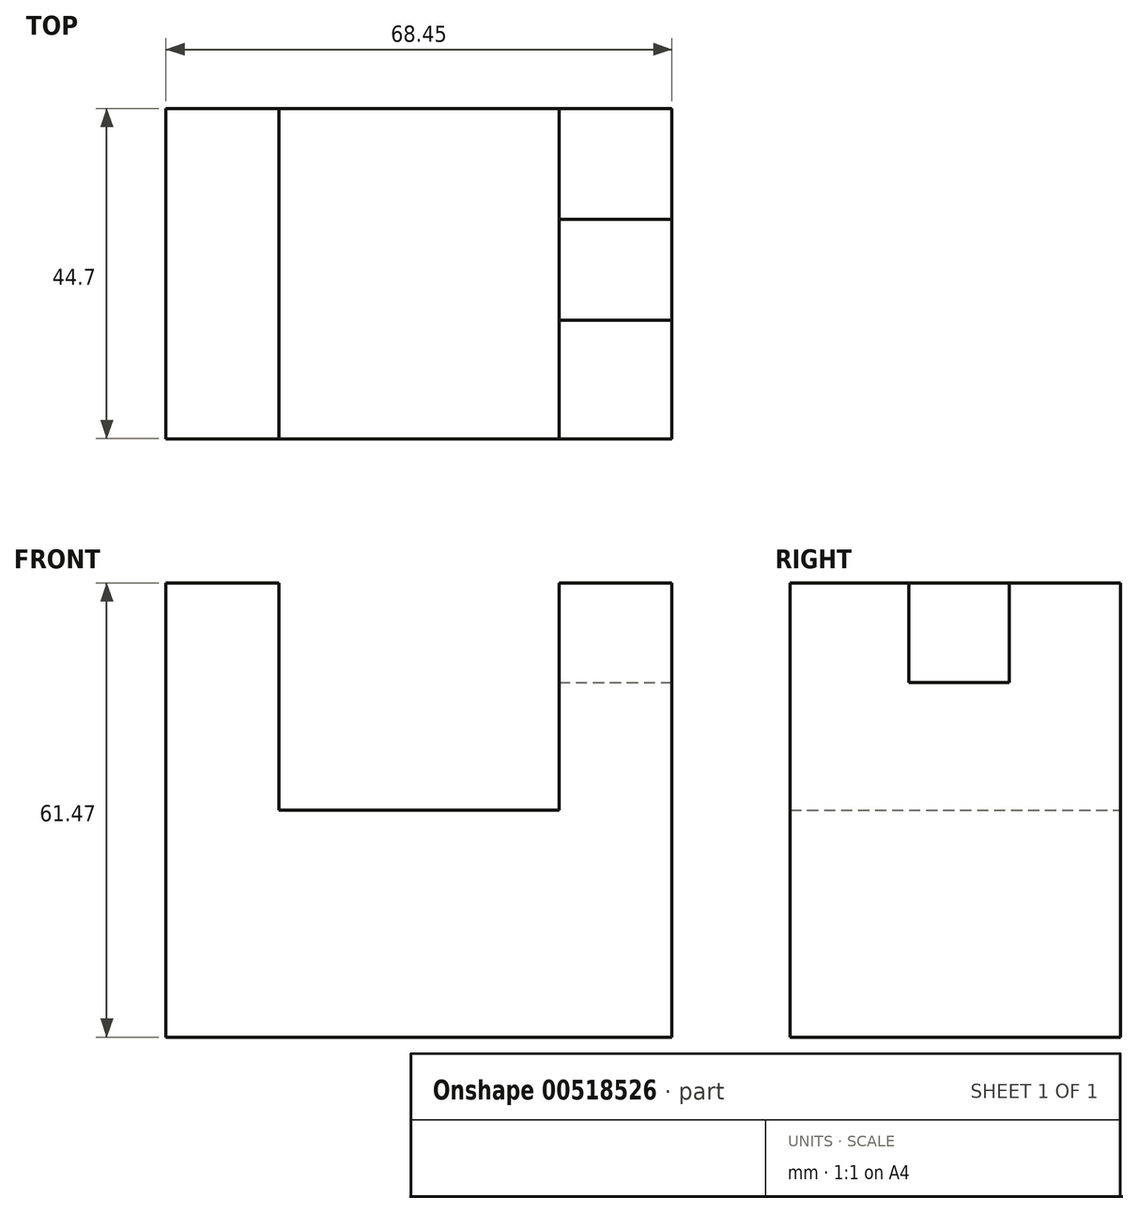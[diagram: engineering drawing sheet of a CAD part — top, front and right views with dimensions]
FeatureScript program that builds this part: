
annotation { "Feature Type Name" : "Feature", "Feature Type Description" : "" }
export const myFeature = defineFeature(function(context is Context, id is Id, definition is map)
    precondition{}
    {
        {
            var Q0;
            Q0=qCreatedBy(makeId("Front.planeOp"),FACE);
            var sketch = newSketch(context, id + "F0", { "sketchPlane" : qUnion([Q0])});
            skLineSegment(sketch, "E0.bottom", {"start": v(0, 0) * mm, "end": v(68.45, 0) * mm});
            skLineSegment(sketch, "E0.top", {"start": v(0, 61.47) * mm, "end": v(15.28, 61.47) * mm});
            skLineSegment(sketch, "E0.left", {"start": v(0, 0) * mm, "end": v(0, 61.47) * mm});
            skLineSegment(sketch, "E0.right", {"start": v(68.45, 0) * mm, "end": v(68.45, 61.47) * mm});
            skPoint(sketch, "E1.firstSnap0", {"position": v(0, 30.74) * mm});
            skLineSegment(sketch, "E1.bottom", {"start": v(15.28, 30.74) * mm, "end": v(53.16, 30.74) * mm});
            skLineSegment(sketch, "E1.left", {"start": v(15.28, 30.74) * mm, "end": v(15.28, 61.47) * mm});
            skLineSegment(sketch, "E1.right", {"start": v(53.16, 30.74) * mm, "end": v(53.16, 61.47) * mm});
            skLineSegment(sketch, "E2.trimOffspring", {"start": v(53.16, 61.47) * mm, "end": v(68.45, 61.47) * mm});
            skSolve(sketch);
        }
        {
            var Q0;
            Q0 = qSketchRegion(id + "F0", true);
            extrude(context, id + "F1", {"entities" : qUnion([Q0]), "depth" : 25.4 * mm, "offsetDistance" : 25.4 * mm});
        }
        {
            var Q0;
            Q0=makeQuery(id+"F1.opExtrude","CAP_FACE",FACE,{"disambiguationData":[OSD([sQuery(id+"F0.wireOp",EDGE,"E0.bottom"),sQuery(id+"F0.wireOp",EDGE,"E0.top"),sQuery(id+"F0.wireOp",EDGE,"E0.left"),sQuery(id+"F0.wireOp",EDGE,"E0.right"),sQuery(id+"F0.wireOp",EDGE,"E1.bottom"),sQuery(id+"F0.wireOp",EDGE,"E1.left"),sQuery(id+"F0.wireOp",EDGE,"E1.right"),sQuery(id+"F0.wireOp",EDGE,"E2.trimOffspring")])],"isStart":false});
            extrude(context, id + "F2", {"entities" : qUnion([Q0]), "operationType" : NewBodyOperationType.ADD, "depth" : 19.3 * mm, "offsetDistance" : 25.4 * mm});
        }
        {
            var Q0;
            {var subQ0=sQuery(id+"F0.wireOp",EDGE,"E2.trimOffspring");Q0=makeQuery(id+"F2.boolean.opBoolean","MERGE",FACE,{"derivedFrom":[makeQuery(id+"F1.opExtrude","SWEPT_FACE",FACE,{"disambiguationData":[OSD([subQ0])]}),makeQuery(id+"F2.opExtrude","SWEPT_FACE",FACE,{"disambiguationData":[OSD([subQ0])]})]});}
            var sketch = newSketch(context, id + "F3", { "sketchPlane" : qUnion([Q0])});
            skLineSegment(sketch, "E3.bottom", {"start": v(53.16, -28.67) * mm, "end": v(68.45, -28.67) * mm});
            skLineSegment(sketch, "E3.top", {"start": v(53.16, -15.04) * mm, "end": v(68.45, -15.04) * mm});
            skLineSegment(sketch, "E3.left", {"start": v(53.16, -28.67) * mm, "end": v(53.16, -15.04) * mm});
            skLineSegment(sketch, "E3.right", {"start": v(68.45, -28.67) * mm, "end": v(68.45, -15.04) * mm});
            skSolve(sketch);
        }
        {
            var Q0;
            Q0=makeQuery(id+"F3.imprint","IMPRINT",FACE,{"disambiguationData":[TD([[makeQuery(id+"F3.imprint","IMPRINT",EDGE,{"derivedFrom":sQuery(id+"F3.wireOp",EDGE,"E3.bottom")}),1.0]])]});
            extrude(context, id + "F4", {"entities" : qUnion([Q0]), "operationType" : NewBodyOperationType.REMOVE, "oppositeDirection" : true, "depth" : 13.46 * mm, "offsetDistance" : 25.4 * mm});
        }
    });
